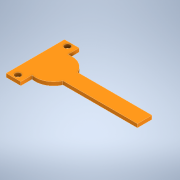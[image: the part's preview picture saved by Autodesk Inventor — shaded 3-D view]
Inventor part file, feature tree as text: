
AUTODESK INVENTOR PART (.ipt)
format: ipt  version: 2021 (Build 250183000, 183)  size: 123,904 bytes
history: native  units: mm
features: other x1, extrude x1, sketch x1
ambient origin geometry x8: Origin, YZ Plane, XZ Plane, XY Plane, X Axis, Y Axis, Z Axis, Center Point
bodies: Solid1 (feature_tree)
feature tree (3):
  other  "<userpath>\Documents\Semestre8\Robótica\Proyecto-Rob\Piezas\ParámetrosGripper.xlsx"
  extrude  "Extrusion1"  Depth=20.0mm
  sketch  "Sketch1"  dims[d0=20.0mm d1=20.0mm d2=80.0mm d3=150.0mm d5=50.0mm d6=15.0mm d7=8.0mm d8=6.0mm d9=8.0mm d10=6.0mm d11=5.0mm d12=0.0mm]
